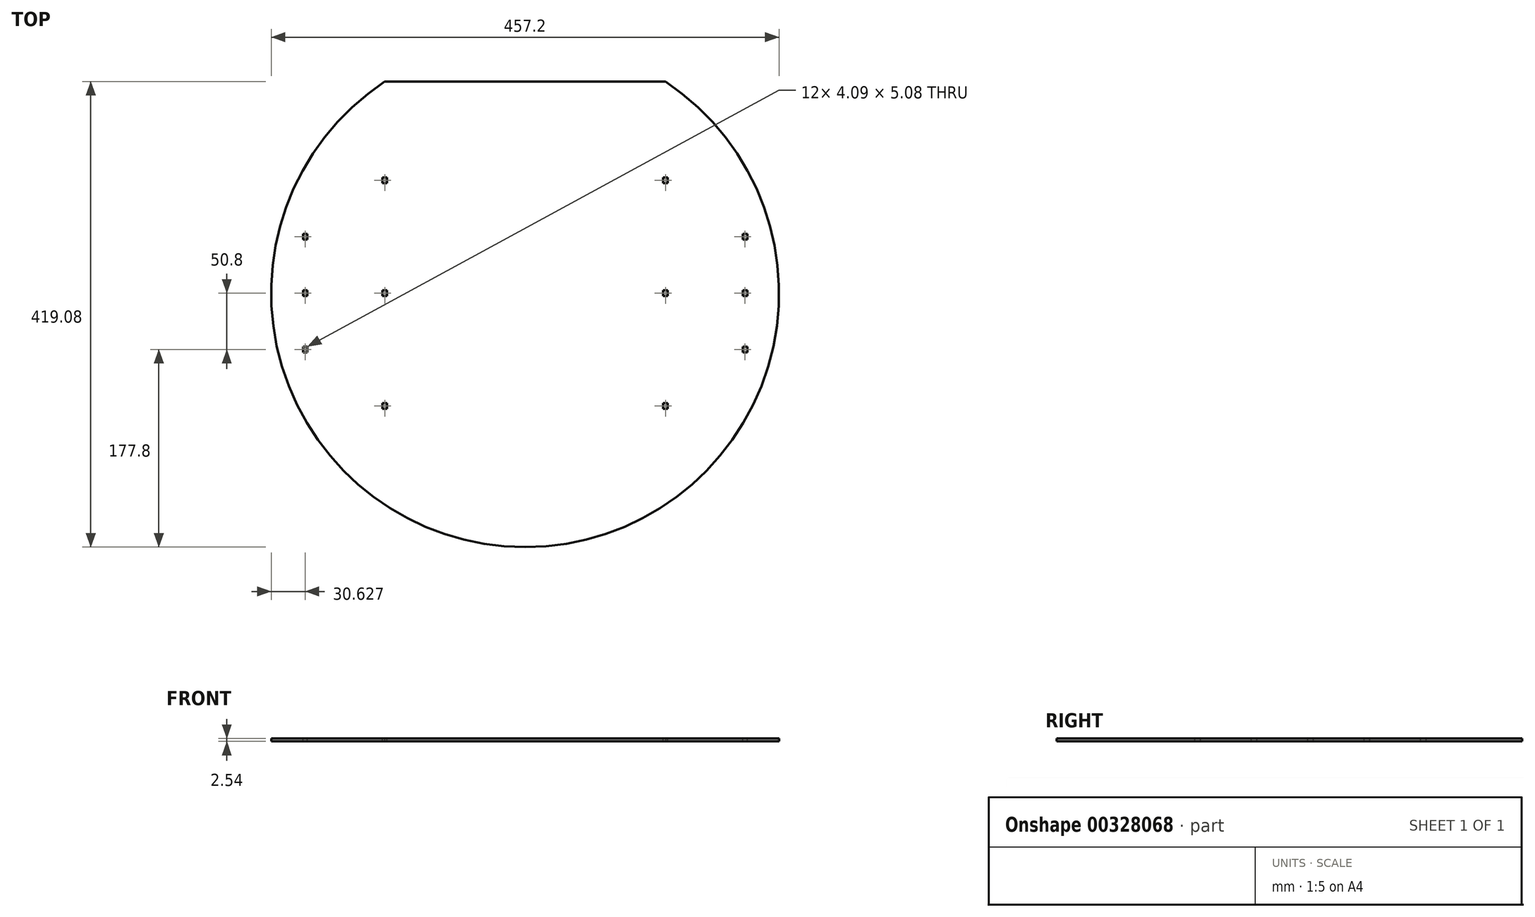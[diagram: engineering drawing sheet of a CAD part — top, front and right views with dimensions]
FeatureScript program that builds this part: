
annotation { "Feature Type Name" : "Feature", "Feature Type Description" : "" }
export const myFeature = defineFeature(function(context is Context, id is Id, definition is map)
    precondition{}
    {
        {
            var Q0;
            Q0=qCreatedBy(makeId("Top.planeOp"),FACE);
            var sketch = newSketch(context, id + "F0", { "sketchPlane" : qUnion([Q0])});
            skArc(sketch, "E0", {"start": v(-126.4, 190.48) * mm, "mid": v(0, -228.6) * mm, "end": v(126.4, 190.48) * mm});
            skLineSegment(sketch, "E1", {"start": v(-126.4, 190.48) * mm, "end": v(126.4, 190.48) * mm});
            skSolve(sketch);
        }
        {
            var Q0;
            Q0=makeQuery(id+"F0.imprint","IMPRINT",FACE,{"disambiguationData":[TD([[makeQuery(id+"F0.imprint","IMPRINT",EDGE,{"derivedFrom":sQuery(id+"F0.wireOp",EDGE,"E0")}),1.0]])]});
            extrude(context, id + "F1", {"entities" : qUnion([Q0]), "depth" : 2.54 * mm});
        }
        {
            var Q0;
            Q0=makeQuery(id+"F1.opExtrude","CAP_FACE",FACE,{"disambiguationData":[OSD([sQuery(id+"F0.wireOp",EDGE,"E0")])],"isStart":false});
            var sketch = newSketch(context, id + "F2", { "sketchPlane" : qUnion([Q0])});
            skLineSegment(sketch, "E2.bottom", {"start": v(-195.93, -2.54) * mm, "end": v(-200.02, -2.54) * mm});
            skLineSegment(sketch, "E2.top", {"start": v(-195.93, 2.54) * mm, "end": v(-200.02, 2.54) * mm});
            skLineSegment(sketch, "E2.left", {"start": v(-195.93, -2.54) * mm, "end": v(-195.93, 2.54) * mm});
            skLineSegment(sketch, "E2.right", {"start": v(-200.02, -2.54) * mm, "end": v(-200.02, 2.54) * mm});
            skPoint(sketch, "E2.middle", {"position": v(-197.97, 0) * mm});
            skLineSegment(sketch, "E3.bottom", {"start": v(-124.32, -2.54) * mm, "end": v(-128.4, -2.54) * mm});
            skLineSegment(sketch, "E3.top", {"start": v(-124.32, 2.54) * mm, "end": v(-128.4, 2.54) * mm});
            skLineSegment(sketch, "E3.left", {"start": v(-124.32, -2.54) * mm, "end": v(-124.32, 2.54) * mm});
            skLineSegment(sketch, "E3.right", {"start": v(-128.4, -2.54) * mm, "end": v(-128.4, 2.54) * mm});
            skPoint(sketch, "E3.middle", {"position": v(-126.36, 0) * mm});
            skLineSegment(sketch, "E4.bottom", {"start": v(-195.93, 48.26) * mm, "end": v(-200.02, 48.26) * mm});
            skLineSegment(sketch, "E4.top", {"start": v(-195.93, 53.34) * mm, "end": v(-200.02, 53.34) * mm});
            skLineSegment(sketch, "E4.left", {"start": v(-195.93, 48.26) * mm, "end": v(-195.93, 53.34) * mm});
            skLineSegment(sketch, "E4.right", {"start": v(-200.02, 48.26) * mm, "end": v(-200.02, 53.34) * mm});
            skPoint(sketch, "E4.middle", {"position": v(-197.97, 50.8) * mm});
            skLineSegment(sketch, "E5.bottom", {"start": v(-195.93, -48.26) * mm, "end": v(-200.02, -48.26) * mm});
            skLineSegment(sketch, "E5.top", {"start": v(-195.93, -53.34) * mm, "end": v(-200.02, -53.34) * mm});
            skLineSegment(sketch, "E5.left", {"start": v(-195.93, -48.26) * mm, "end": v(-195.93, -53.34) * mm});
            skLineSegment(sketch, "E5.right", {"start": v(-200.02, -48.26) * mm, "end": v(-200.02, -53.34) * mm});
            skPoint(sketch, "E5.middle", {"position": v(-197.97, -50.8) * mm});
            skLineSegment(sketch, "E6.bottom", {"start": v(-124.32, 99.06) * mm, "end": v(-128.4, 99.06) * mm});
            skLineSegment(sketch, "E6.top", {"start": v(-124.32, 104.14) * mm, "end": v(-128.4, 104.14) * mm});
            skLineSegment(sketch, "E6.left", {"start": v(-124.32, 99.06) * mm, "end": v(-124.32, 104.14) * mm});
            skLineSegment(sketch, "E6.right", {"start": v(-128.4, 99.06) * mm, "end": v(-128.4, 104.14) * mm});
            skPoint(sketch, "E6.middle", {"position": v(-126.36, 101.6) * mm});
            skLineSegment(sketch, "E7.bottom", {"start": v(-124.32, -104.14) * mm, "end": v(-128.4, -104.14) * mm});
            skLineSegment(sketch, "E7.top", {"start": v(-124.32, -99.06) * mm, "end": v(-128.4, -99.06) * mm});
            skLineSegment(sketch, "E7.left", {"start": v(-124.32, -104.14) * mm, "end": v(-124.32, -99.06) * mm});
            skLineSegment(sketch, "E7.right", {"start": v(-128.4, -104.14) * mm, "end": v(-128.4, -99.06) * mm});
            skPoint(sketch, "E7.middle", {"position": v(-126.36, -101.6) * mm});
            skLineSegment(sketch, "E8", {"start": v(0, 0) * mm, "end": v(0, -180.02) * mm, "construction": true});
            skLineSegment(sketch, "E9.MirrorCS", {"start": v(195.93, -2.54) * mm, "end": v(200.02, -2.54) * mm});
            skLineSegment(sketch, "E10.MirrorCS", {"start": v(195.93, 2.54) * mm, "end": v(200.02, 2.54) * mm});
            skLineSegment(sketch, "E11.MirrorCS", {"start": v(195.93, -48.26) * mm, "end": v(200.02, -48.26) * mm});
            skLineSegment(sketch, "E12.MirrorCS", {"start": v(200.02, 48.26) * mm, "end": v(200.02, 53.34) * mm});
            skLineSegment(sketch, "E13.MirrorCS", {"start": v(195.93, -2.54) * mm, "end": v(195.93, 2.54) * mm});
            skLineSegment(sketch, "E14.MirrorCS", {"start": v(200.02, -2.54) * mm, "end": v(200.02, 2.54) * mm});
            skLineSegment(sketch, "E15.MirrorCS", {"start": v(124.32, -2.54) * mm, "end": v(128.4, -2.54) * mm});
            skLineSegment(sketch, "E16.MirrorCS", {"start": v(124.32, 2.54) * mm, "end": v(128.4, 2.54) * mm});
            skLineSegment(sketch, "E17.MirrorCS", {"start": v(124.32, -2.54) * mm, "end": v(124.32, 2.54) * mm});
            skLineSegment(sketch, "E18.MirrorCS", {"start": v(128.4, -2.54) * mm, "end": v(128.4, 2.54) * mm});
            skLineSegment(sketch, "E19.MirrorCS", {"start": v(124.32, -99.06) * mm, "end": v(128.4, -99.06) * mm});
            skLineSegment(sketch, "E20.MirrorCS", {"start": v(124.32, 104.14) * mm, "end": v(128.4, 104.14) * mm});
            skLineSegment(sketch, "E21.MirrorCS", {"start": v(128.4, -104.14) * mm, "end": v(128.4, -99.06) * mm});
            skLineSegment(sketch, "E22.MirrorCS", {"start": v(124.32, -104.14) * mm, "end": v(124.32, -99.06) * mm});
            skLineSegment(sketch, "E23.MirrorCS", {"start": v(124.32, 99.06) * mm, "end": v(124.32, 104.14) * mm});
            skLineSegment(sketch, "E24.MirrorCS", {"start": v(195.93, -53.34) * mm, "end": v(200.02, -53.34) * mm});
            skLineSegment(sketch, "E25.MirrorCS", {"start": v(195.93, 48.26) * mm, "end": v(195.93, 53.34) * mm});
            skLineSegment(sketch, "E26.MirrorCS", {"start": v(195.93, 48.26) * mm, "end": v(200.02, 48.26) * mm});
            skLineSegment(sketch, "E27.MirrorCS", {"start": v(128.4, 99.06) * mm, "end": v(128.4, 104.14) * mm});
            skLineSegment(sketch, "E28.MirrorCS", {"start": v(195.93, 53.34) * mm, "end": v(200.02, 53.34) * mm});
            skLineSegment(sketch, "E29.MirrorCS", {"start": v(124.32, 99.06) * mm, "end": v(128.4, 99.06) * mm});
            skLineSegment(sketch, "E30.MirrorCS", {"start": v(195.93, -48.26) * mm, "end": v(195.93, -53.34) * mm});
            skLineSegment(sketch, "E31.MirrorCS", {"start": v(124.32, -104.14) * mm, "end": v(128.4, -104.14) * mm});
            skLineSegment(sketch, "E32.MirrorCS", {"start": v(200.02, -48.26) * mm, "end": v(200.02, -53.34) * mm});
            skPoint(sketch, "E33.MirrorP", {"position": v(197.97, 0) * mm});
            skPoint(sketch, "E34.MirrorP", {"position": v(126.36, -101.6) * mm});
            skPoint(sketch, "E35.MirrorP", {"position": v(126.36, 0) * mm});
            skPoint(sketch, "E36.MirrorP", {"position": v(197.97, 50.8) * mm});
            skPoint(sketch, "E37.MirrorP", {"position": v(197.97, -50.8) * mm});
            skPoint(sketch, "E38.MirrorP", {"position": v(126.36, 101.6) * mm});
            skLineSegment(sketch, "E39", {"start": v(-126.36, 101.6) * mm, "end": v(-126.36, -101.6) * mm, "construction": true});
            skLineSegment(sketch, "E40", {"start": v(126.36, 101.6) * mm, "end": v(126.36, 0) * mm, "construction": true});
            skLineSegment(sketch, "E41", {"start": v(126.36, 0) * mm, "end": v(126.36, -101.6) * mm, "construction": true});
            skLineSegment(sketch, "E42", {"start": v(-195.93, 0) * mm, "end": v(-128.4, 0) * mm, "construction": true});
            skSolve(sketch);
        }
        {
            var Q0;
            Q0 = qSketchRegion(id + "F2", true);
            extrude(context, id + "F3", {"entities" : qUnion([Q0]), "operationType" : NewBodyOperationType.REMOVE, "oppositeDirection" : true, "depth" : 25.4 * mm});
        }
        {
            var Q0;
            Q0=makeQuery(id+"F2.imprint","IMPRINT",FACE,{"disambiguationData":[TD([[makeQuery(id+"F2.imprint","IMPRINT",EDGE,{"derivedFrom":sQuery(id+"F2.wireOp",EDGE,"E20.MirrorCS")}),-1.0]])]});
            var Q1;
            Q1=makeQuery(id+"F2.imprint","IMPRINT",FACE,{"disambiguationData":[TD([[makeQuery(id+"F2.imprint","IMPRINT",EDGE,{"derivedFrom":sQuery(id+"F2.wireOp",EDGE,"E12.MirrorCS")}),1.0]])]});
            var Q2;
            Q2=makeQuery(id+"F2.imprint","IMPRINT",FACE,{"disambiguationData":[TD([[makeQuery(id+"F2.imprint","IMPRINT",EDGE,{"derivedFrom":sQuery(id+"F2.wireOp",EDGE,"E15.MirrorCS")}),1.0]])]});
            var Q3;
            Q3=makeQuery(id+"F2.imprint","IMPRINT",FACE,{"disambiguationData":[TD([[makeQuery(id+"F2.imprint","IMPRINT",EDGE,{"derivedFrom":sQuery(id+"F2.wireOp",EDGE,"E9.MirrorCS")}),1.0]])]});
            var Q4;
            Q4=makeQuery(id+"F2.imprint","IMPRINT",FACE,{"disambiguationData":[TD([[makeQuery(id+"F2.imprint","IMPRINT",EDGE,{"derivedFrom":sQuery(id+"F2.wireOp",EDGE,"E11.MirrorCS")}),-1.0]])]});
            var Q5;
            Q5=makeQuery(id+"F2.imprint","IMPRINT",FACE,{"disambiguationData":[TD([[makeQuery(id+"F2.imprint","IMPRINT",EDGE,{"derivedFrom":sQuery(id+"F2.wireOp",EDGE,"E19.MirrorCS")}),-1.0]])]});
            extrude(context, id + "F4", {"entities" : qUnion([Q0, Q1, Q2, Q3, Q4, Q5]), "operationType" : NewBodyOperationType.REMOVE, "oppositeDirection" : true, "depth" : 25.4 * mm});
        }
    });
